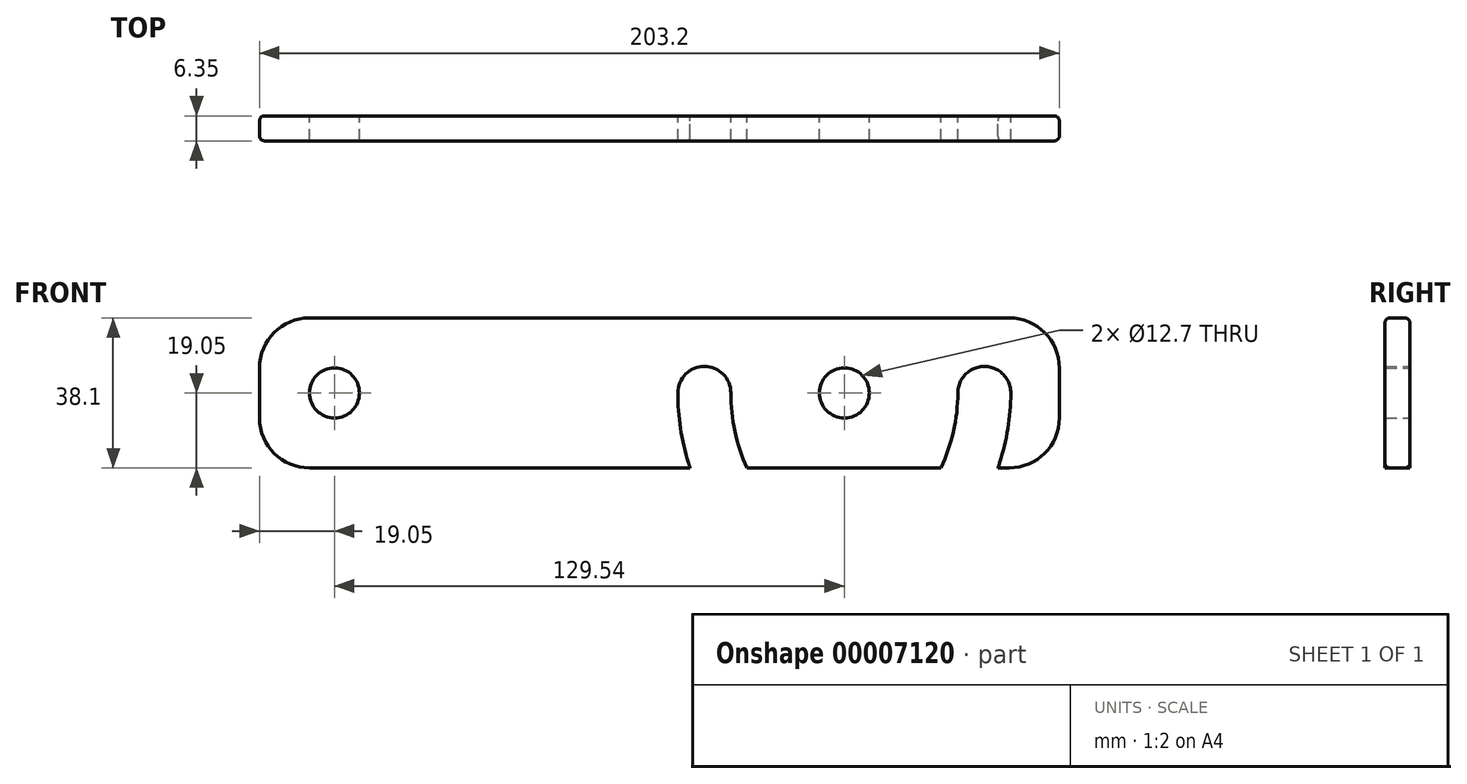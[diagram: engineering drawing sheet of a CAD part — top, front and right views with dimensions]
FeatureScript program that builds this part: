
annotation { "Feature Type Name" : "Feature", "Feature Type Description" : "" }
export const myFeature = defineFeature(function(context is Context, id is Id, definition is map)
    precondition{}
    {
        {
            var Q0;
            Q0=qCreatedBy(makeId("Front.planeOp"),FACE);
            var sketch = newSketch(context, id + "F0", { "sketchPlane" : qUnion([Q0])});
            skLineSegment(sketch, "E0.rect.bottom", {"start": v(88.9, 19.05) * mm, "end": v(-88.9, 19.05) * mm});
            skLineSegment(sketch, "E0.rect.top", {"start": v(88.9, -19.05) * mm, "end": v(86.04, -19.05) * mm});
            skLineSegment(sketch, "E0.rect.left", {"start": v(101.6, 6.35) * mm, "end": v(101.6, -6.35) * mm});
            skLineSegment(sketch, "E0.rect.right", {"start": v(-101.6, 6.35) * mm, "end": v(-101.6, -6.35) * mm});
            skPoint(sketch, "E0.rect.middle", {"position": v(0, 0) * mm});
            skPoint(sketch, "E1.visualSharp", {"position": v(-101.6, 19.05) * mm});
            skArc(sketch, "E1.filletArc", {"start": v(-88.9, 19.05) * mm, "mid": v(-97.88, 15.33) * mm, "end": v(-101.6, 6.35) * mm});
            skPoint(sketch, "E2.visualSharp", {"position": v(-101.6, -19.05) * mm});
            skArc(sketch, "E2.filletArc", {"start": v(-101.6, -6.35) * mm, "mid": v(-97.88, -15.33) * mm, "end": v(-88.9, -19.05) * mm});
            skPoint(sketch, "E3.visualSharp", {"position": v(101.6, -19.05) * mm});
            skArc(sketch, "E3.filletArc", {"start": v(88.9, -19.05) * mm, "mid": v(97.88, -15.33) * mm, "end": v(101.6, -6.35) * mm});
            skPoint(sketch, "E4.visualSharp", {"position": v(101.6, 19.05) * mm});
            skArc(sketch, "E4.filletArc", {"start": v(101.6, 6.35) * mm, "mid": v(97.88, 15.33) * mm, "end": v(88.9, 19.05) * mm});
            skCircle(sketch, "E5", {"center": v(-82.55, 0) * mm, "radius": 6.35 * mm});
            skLineSegment(sketch, "E6", {"start": v(0, 0) * mm, "end": v(0, 44.49) * mm, "construction": true});
            skCircle(sketch, "E7", {"center": v(47, 0) * mm, "radius": 6.35 * mm});
            skCircle(sketch, "E8", {"center": v(82.55, 0) * mm, "radius": 6.73 * mm});
            skPoint(sketch, "E9", {"position": v(64.77, 0) * mm});
            skPoint(sketch, "E10", {"position": v(89.28, 0) * mm});
            skPoint(sketch, "E11", {"position": v(71.49, -19.05) * mm});
            skPoint(sketch, "E12", {"position": v(86.04, -19.05) * mm});
            skPoint(sketch, "E13", {"position": v(75.82, 0) * mm});
            skLineSegment(sketch, "E14", {"start": v(86.04, -19.05) * mm, "end": v(-88.9, -19.05) * mm});
            skArc(sketch, "E15", {"start": v(86.04, -19.05) * mm, "mid": v(88.43, -9.66) * mm, "end": v(89.28, 0) * mm});
            skArc(sketch, "E16", {"start": v(71.49, -19.05) * mm, "mid": v(74.72, -9.77) * mm, "end": v(75.82, 0) * mm});
            skPoint(sketch, "E17", {"position": v(34.85, 19.05) * mm});
            skPoint(sketch, "E18", {"position": v(10.6, 19.05) * mm});
            skLineSegment(sketch, "E19", {"start": v(47, 0) * mm, "end": v(18.16, 0) * mm});
            skCircle(sketch, "E20", {"center": v(11.43, 0) * mm, "radius": 6.73 * mm});
            skArc(sketch, "E21", {"start": v(18.16, 0) * mm, "mid": v(19.2, -9.74) * mm, "end": v(22.23, -19.05) * mm});
            skLineSegment(sketch, "E22", {"start": v(18.16, 0) * mm, "end": v(11.43, 0) * mm});
            skArc(sketch, "E23", {"start": v(4.7, 0) * mm, "mid": v(5.48, -9.65) * mm, "end": v(7.8, -19.05) * mm});
            skSolve(sketch);
        }
        {
            var Q0;
            Q0=makeQuery(id+"F0.imprint","IMPRINT",FACE,{"disambiguationData":[TD([[makeQuery(id+"F0.imprint","IMPRINT",EDGE,{"derivedFrom":sQuery(id+"F0.wireOp",EDGE,"E0.rect.bottom")}),1.0]])]});
            extrude(context, id + "F1", {"entities" : qUnion([Q0]), "depth" : 6.35 * mm});
        }
        {
            var Q0;
            Q0=makeQuery(id+"F1.opExtrude","CAP_EDGE",EDGE,{"disambiguationData":[OSD([sQuery(id+"F0.wireOp",EDGE,"E0.rect.bottom")])],"isStart":false});
            var Q1;
            Q1=makeQuery(id+"F1.opExtrude","CAP_EDGE",EDGE,{"disambiguationData":[OSD([sQuery(id+"F0.wireOp",EDGE,"E0.rect.bottom")])],"isStart":true});
            fillet(context, id + "F2", {"entities" : qUnion([Q0, Q1]), "radius" : 1.27 * mm, "tangentPropagation" : true, "allowEdgeOverflow" : false});
        }
    });
